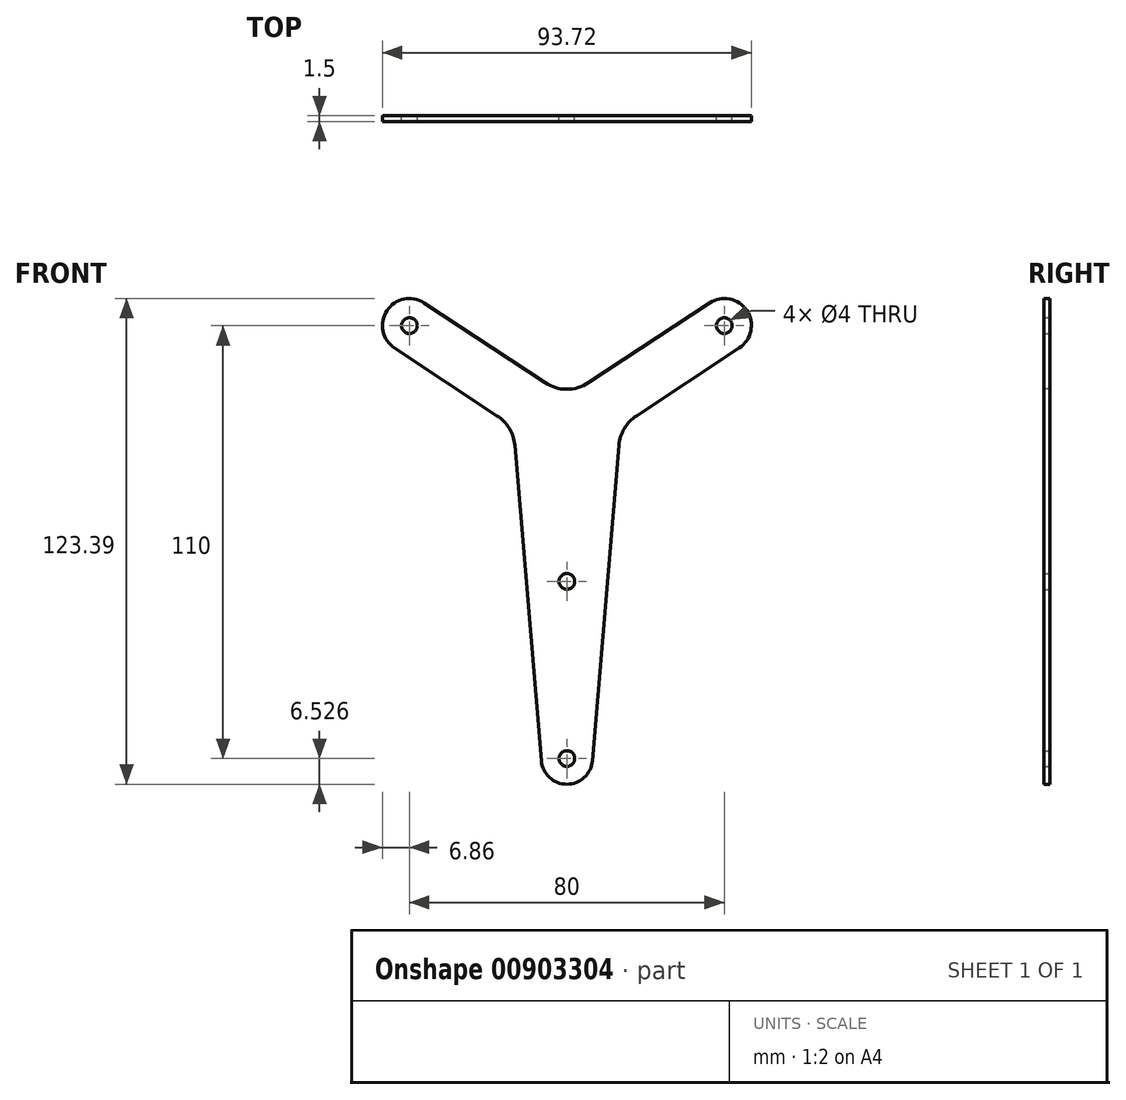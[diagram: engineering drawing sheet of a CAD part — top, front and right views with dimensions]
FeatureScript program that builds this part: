
annotation { "Feature Type Name" : "Feature", "Feature Type Description" : "" }
export const myFeature = defineFeature(function(context is Context, id is Id, definition is map)
    precondition{}
    {
        {
            var Q0;
            Q0=qCreatedBy(makeId("Front.planeOp"),FACE);
            var sketch = newSketch(context, id + "F0", { "sketchPlane" : qUnion([Q0])});
            skArc(sketch, "E0", {"start": v(-6.5, 0) * mm, "mid": v(0, -5.98) * mm, "end": v(6.5, 0) * mm});
            skLineSegment(sketch, "E1", {"start": v(-6.5, 0) * mm, "end": v(-13.64, 84.96) * mm});
            skArc(sketch, "E2", {"start": v(-43.78, 104.82) * mm, "mid": v(-45.73, 114.32) * mm, "end": v(-36.22, 116.28) * mm});
            skLineSegment(sketch, "E3.MirrorCS", {"start": v(6.5, 0) * mm, "end": v(13.64, 84.96) * mm});
            skArc(sketch, "E4.MirrorCS", {"start": v(43.78, 104.82) * mm, "mid": v(45.73, 114.32) * mm, "end": v(36.22, 116.28) * mm});
            skCircle(sketch, "E5", {"center": v(0, 0.55) * mm, "radius": 2 * mm});
            skCircle(sketch, "E6", {"center": v(-40, 110.55) * mm, "radius": 2 * mm});
            skCircle(sketch, "E7", {"center": v(40, 110.55) * mm, "radius": 2 * mm});
            skCircle(sketch, "E8", {"center": v(0, 45.55) * mm, "radius": 2 * mm});
            skLineSegment(sketch, "E9", {"start": v(-13.64, 84.96) * mm, "end": v(-43.78, 104.82) * mm});
            skLineSegment(sketch, "E10", {"start": v(13.64, 84.96) * mm, "end": v(43.78, 104.82) * mm});
            skLineSegment(sketch, "E11", {"start": v(-36.22, 116.28) * mm, "end": v(0, 92.41) * mm});
            skLineSegment(sketch, "E12", {"start": v(0, 92.41) * mm, "end": v(36.22, 116.28) * mm});
            skSolve(sketch);
        }
        {
            var Q0;
            Q0=makeQuery(id+"F0.imprint","IMPRINT",FACE,{"disambiguationData":[TD([[makeQuery(id+"F0.imprint","IMPRINT",EDGE,{"derivedFrom":sQuery(id+"F0.wireOp",EDGE,"E0")}),1.0]])]});
            extrude(context, id + "F1", {"entities" : qUnion([Q0]), "depth" : 1.5 * mm, "offsetDistance" : 25 * mm});
        }
        {
            var Q0;
            Q0=makeQuery(id+"F1.opExtrude","SWEPT_EDGE",EDGE,{"disambiguationData":[OSD([sQuery(id+"F0.wireOp",EDGE,"E11"),sQuery(id+"F0.wireOp",EDGE,"E12")])]});
            var Q1;
            Q1=makeQuery(id+"F1.opExtrude","SWEPT_EDGE",EDGE,{"disambiguationData":[OSD([sQuery(id+"F0.wireOp",EDGE,"E1"),sQuery(id+"F0.wireOp",EDGE,"E9")])]});
            var Q2;
            Q2=makeQuery(id+"F1.opExtrude","SWEPT_EDGE",EDGE,{"disambiguationData":[OSD([sQuery(id+"F0.wireOp",EDGE,"E3.MirrorCS"),sQuery(id+"F0.wireOp",EDGE,"E10")])]});
            fillet(context, id + "F2", {"entities" : qUnion([Q0, Q1, Q2]), "radius" : 10 * mm, "tangentPropagation" : true, "allowEdgeOverflow" : false});
        }
    });
